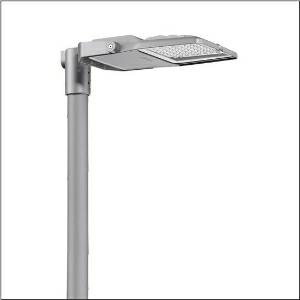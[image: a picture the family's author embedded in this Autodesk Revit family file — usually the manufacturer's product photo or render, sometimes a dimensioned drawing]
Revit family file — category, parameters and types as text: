
# Revit family: floodlight_fl_21_iq_mini___pl64_5xa7772c4e3a_b66a
name_source: partatom
category: Lighting Fixtures
units: mm (PartAtom-declared; Revit-internal decimal feet)

## family parameters
Cut with Voids When Loaded = No
Host = Face
Light Source = No
Part Type = Normal
Room Calculation Point = No
Round Connector Dimension = Use Diameter
Shared = No

## types (1)
- --- (1 x LED, 12280 lm, 87.2 W, 4000K)
    Apparent Load = 87 VA
    CIE Flux Codes = 28 80 98 100 100
    Color Rendering = 70
    Color Temperature = 4000K
    Default Elevation = 1800 mm
    Description = Floodlight FL 21 iQ mini, floodlight, primary light control with lens, of PMMA, primary optical cover: protective disc, of toughened safety glass, transparent, light distribution: PL64, light emission: direct distribution, installation type: surface-mounted, LED, High Power LED, rated luminous flux: 12.280lm, luminous efficacy: 141lm/W, light colour: 740, colour temperature: 4000K, control gear: iQ Street-Remote/DALI, control: Auto-Match, Temp-Guard, Night-Set, Smart-Wire, Desk-Remote (wireless, voltage-free reading and setting of iQ features in the workshop via application-optimized NFC function/RFID function), optimised constant luminous flux control (CLO 2.0), Light-Fading, Lumen-Switch, with terminal, 6-pole, mains connection: 220..240V, AC, 50/60Hz, start of lifetime: 87W, end of service life: 92W, reduction: 40W, luminaire housing, of diecast aluminium, powder-coated, Siteco® metallic grey (DB 702S), corrosivity category C5 mid according to DIN EN ISO 12944, suitable for swimming pools, chlorine-resistant, sealing non-destructively replaceable, please order mast flange separately, mast bracket, of steel, galvanised, powder-coated, protection rating (complete): IP66, insulation class (complete): insulation class II (safety insulation), certification: CE, ENEC, VDE, protection symbol: D, impact resistance: IK08, permissible operating ambient temperature: -40..+40°C, permissible operating ambient temperature for outdoor applications: -40..+50°C, standard: DIN EN 12944, LABS conformity tested according to VDMA 24364:2018-05, packaging unit: 1 piece

Light Distribution: PL64
    Height = 70 mm
    Lamp = 1 x LED
    Lamp Light Flux = 12280 lm
    Lamp Power = 87.2 W
    Lamp count = 1
    Length = 485 mm
    Luminous efficacy = 141 lm/W
    Manufacturer = Siteco
    ModVariant = No
    Model = 5XA7772C4E3A
    Number of Poles = 1
    OnlyDefault = Yes
    Power Factor = 1
    Product Name = Floodlight FL 21 iQ mini | PL64
    Product group = floodlight | pylon annexe
    ProductGroupID = 6201
    Protection Class = Protection class II
    Protection Degree = IP 66
    RLX_Detail_Level = 1
    RLX_Emergency_Light_Flux = 0 lm
    RLX_Emergency_Type = 0
    RLX_Emergency_Type_DB = No
    RlxData = <blob elided: 101409 chars, md5=f3e5975c>
    Socket = socket
    Standby Power = 0 W
    System Light Flux = 12280 lm
    System Power = 87 W
    Type Comments = factory setting: luminous flux: 100 % | dim-lin: 254 | 456 mA
    Type Image = l_1007125.jpg
    URL = http://relux.com
    VarID = @adj_187683
    Voltage = 0 V
    Weight = 0.00 kg
    Width = 337 mm

## geometry (parser evidence)
native form markers: Blend x4, Sweep x12
no freeform markers — native parametric forms only
